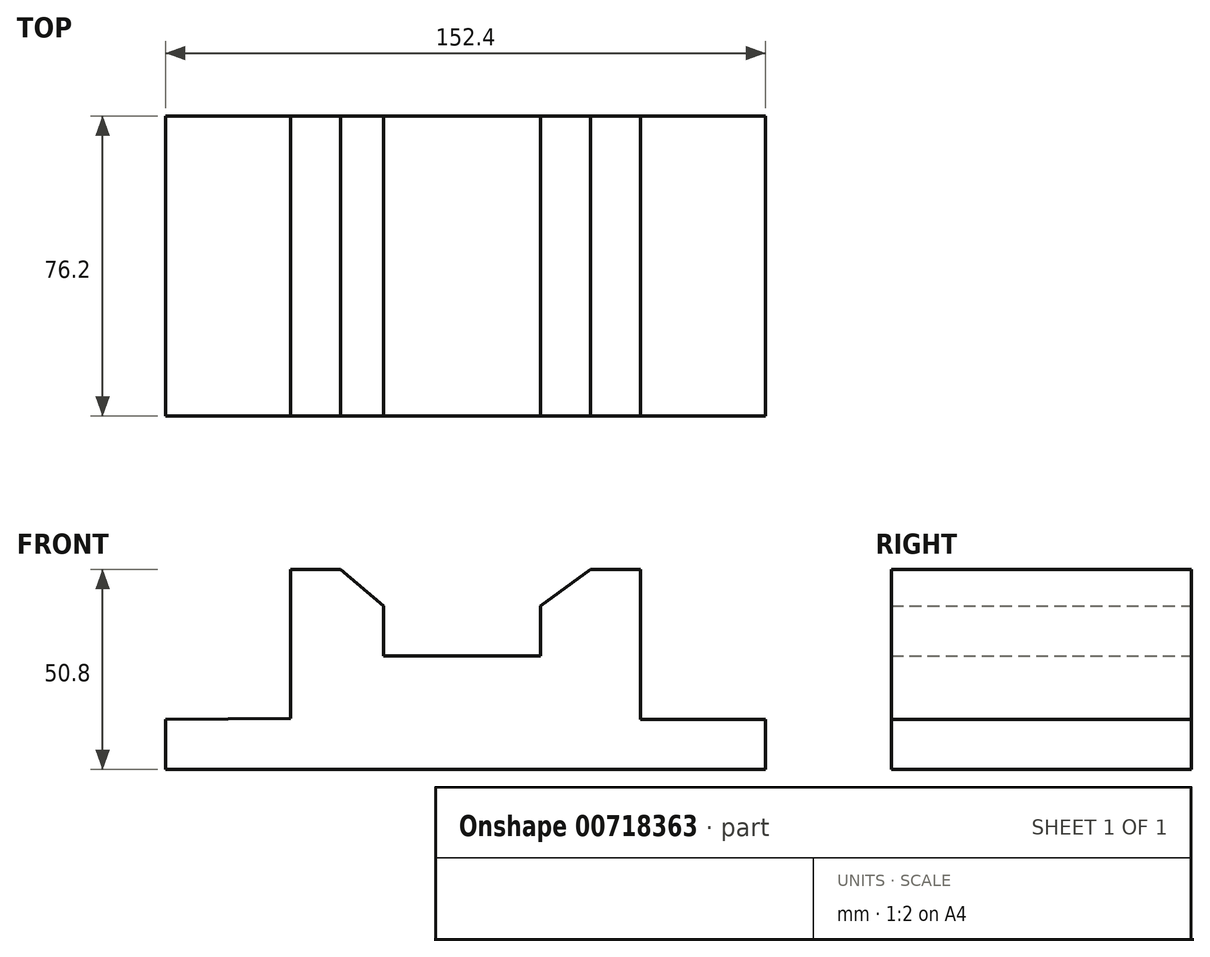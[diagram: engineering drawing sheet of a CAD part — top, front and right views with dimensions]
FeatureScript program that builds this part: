
annotation { "Feature Type Name" : "Feature", "Feature Type Description" : "" }
export const myFeature = defineFeature(function(context is Context, id is Id, definition is map)
    precondition{}
    {
        {
            var Q0;
            Q0=qCreatedBy(makeId("Front.planeOp"),FACE);
            var sketch = newSketch(context, id + "F0", { "sketchPlane" : qUnion([Q0])});
            skLineSegment(sketch, "E0", {"start": v(-65.76, -11.66) * mm, "end": v(-65.76, -24.36) * mm});
            skLineSegment(sketch, "E1", {"start": v(-65.76, -24.36) * mm, "end": v(86.64, -24.36) * mm});
            skLineSegment(sketch, "E2", {"start": v(86.64, -24.36) * mm, "end": v(86.64, -11.66) * mm});
            skLineSegment(sketch, "E3", {"start": v(86.64, -11.66) * mm, "end": v(54.9, -11.66) * mm});
            skLineSegment(sketch, "E4", {"start": v(54.9, -11.66) * mm, "end": v(54.9, 26.44) * mm});
            skLineSegment(sketch, "E5", {"start": v(54.9, 26.44) * mm, "end": v(42.2, 26.44) * mm});
            skLineSegment(sketch, "E6", {"start": v(42.2, 26.44) * mm, "end": v(29.5, 17.15) * mm});
            skLineSegment(sketch, "E7", {"start": v(29.5, 17.15) * mm, "end": v(29.5, 4.45) * mm});
            skLineSegment(sketch, "E8", {"start": v(29.5, 4.45) * mm, "end": v(-10.37, 4.45) * mm});
            skLineSegment(sketch, "E9", {"start": v(-10.37, 4.45) * mm, "end": v(-10.37, 17.15) * mm});
            skLineSegment(sketch, "E10", {"start": v(-10.37, 17.15) * mm, "end": v(-21.3, 26.44) * mm});
            skLineSegment(sketch, "E11", {"start": v(-21.3, 26.44) * mm, "end": v(-34, 26.44) * mm});
            skLineSegment(sketch, "E12", {"start": v(-34, 26.44) * mm, "end": v(-34, -11.41) * mm});
            skLineSegment(sketch, "E13", {"start": v(-34, -11.41) * mm, "end": v(-65.76, -11.66) * mm});
            skSolve(sketch);
        }
        {
            var Q0;
            Q0=makeQuery(id+"F0.imprint","IMPRINT",FACE,{"disambiguationData":[TD([[makeQuery(id+"F0.imprint","IMPRINT",EDGE,{"derivedFrom":sQuery(id+"F0.wireOp",EDGE,"E0")}),1.0]])]});
            extrude(context, id + "F1", {"entities" : qUnion([Q0]), "depth" : 76.2 * mm, "offsetDistance" : 25.4 * mm});
        }
    });
